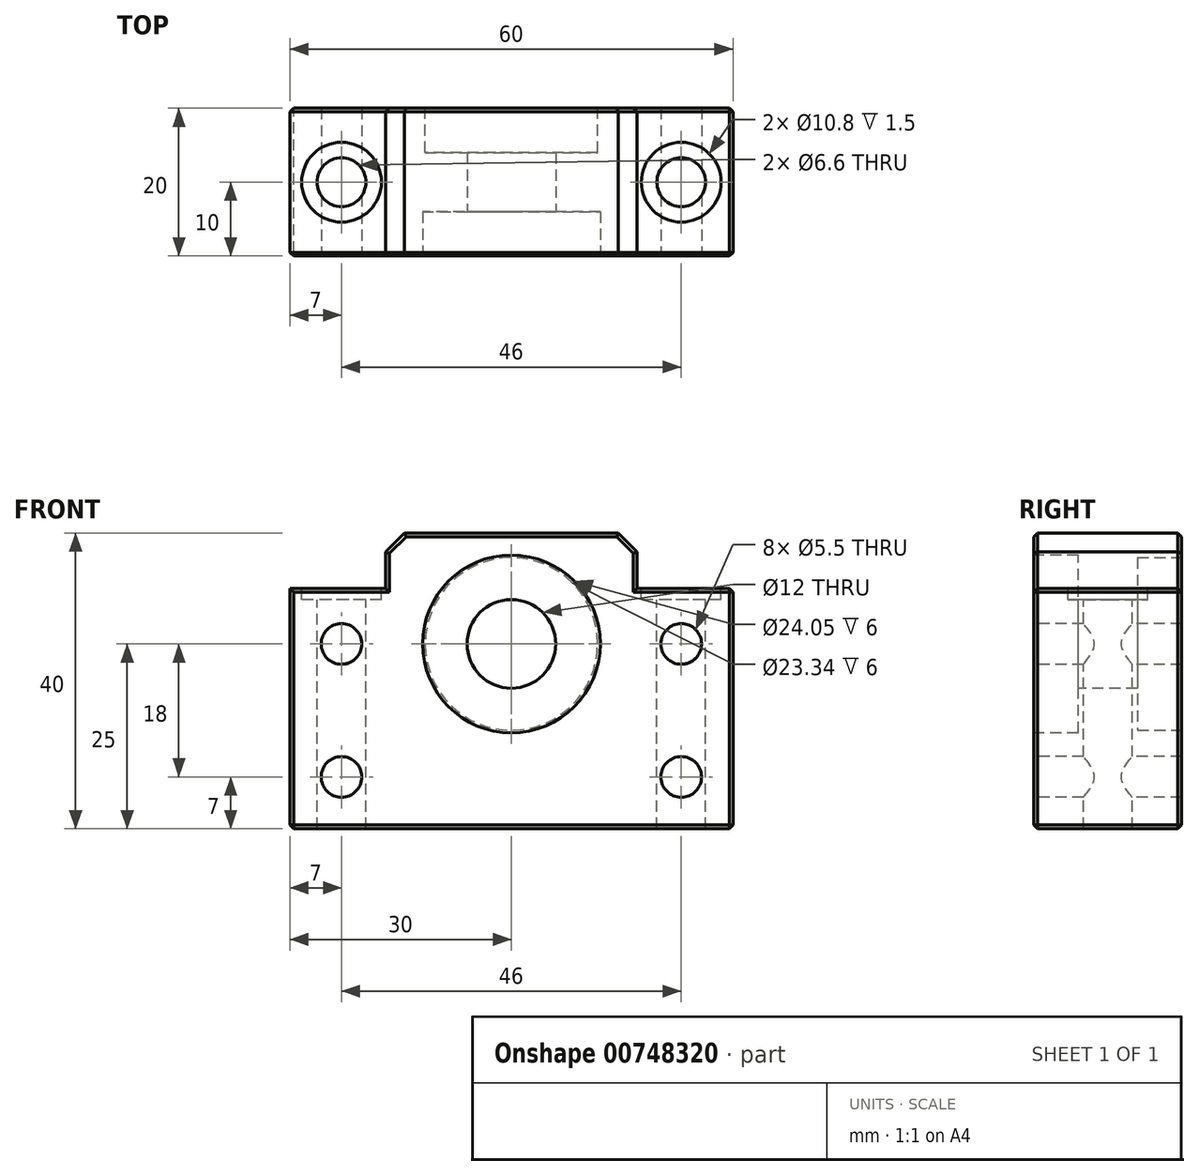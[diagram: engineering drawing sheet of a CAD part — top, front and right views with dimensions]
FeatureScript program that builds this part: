
annotation { "Feature Type Name" : "Feature", "Feature Type Description" : "" }
export const myFeature = defineFeature(function(context is Context, id is Id, definition is map)
    precondition{}
    {
        {
            var Q0;
            Q0=qCreatedBy(makeId("Front.planeOp"),FACE);
            var sketch = newSketch(context, id + "F0", { "sketchPlane" : qUnion([Q0])});
            skLineSegment(sketch, "E0.bottom", {"start": v(30, -16.25) * mm, "end": v(-30, -16.25) * mm});
            skLineSegment(sketch, "E0.top", {"start": v(30, 16.25) * mm, "end": v(17, 16.25) * mm});
            skLineSegment(sketch, "E0.left", {"start": v(30, -16.25) * mm, "end": v(30, 16.25) * mm});
            skLineSegment(sketch, "E0.right", {"start": v(-30, -16.25) * mm, "end": v(-30, 16.25) * mm});
            skPoint(sketch, "E0.middle", {"position": v(0, 0) * mm});
            skLineSegment(sketch, "E1.bottom", {"start": v(17, 23.75) * mm, "end": v(-17, 23.75) * mm});
            skLineSegment(sketch, "E1.left", {"start": v(17, 23.75) * mm, "end": v(17, 16.25) * mm});
            skLineSegment(sketch, "E1.right", {"start": v(-17, 23.75) * mm, "end": v(-17, 16.25) * mm});
            skPoint(sketch, "E1.middle", {"position": v(0, 16.25) * mm});
            skLineSegment(sketch, "E2.trimOffspring", {"start": v(-17, 16.25) * mm, "end": v(-30, 16.25) * mm});
            skSolve(sketch);
        }
        {
            var Q0;
            Q0 = qSketchRegion(id + "F0", true);
            extrude(context, id + "F1", {"entities" : qUnion([Q0]), "depth" : 20 * mm, "offsetDistance" : 25.4 * mm});
        }
        {
            var Q0;
            Q0=makeQuery(id+"F1.opExtrude","CAP_FACE",FACE,{"disambiguationData":[OSD([sQuery(id+"F0.wireOp",EDGE,"E0.bottom"),sQuery(id+"F0.wireOp",EDGE,"E0.top"),sQuery(id+"F0.wireOp",EDGE,"E0.left"),sQuery(id+"F0.wireOp",EDGE,"E0.right"),sQuery(id+"F0.wireOp",EDGE,"E1.bottom"),sQuery(id+"F0.wireOp",EDGE,"E1.left"),sQuery(id+"F0.wireOp",EDGE,"E1.right"),sQuery(id+"F0.wireOp",EDGE,"E2.trimOffspring")])],"isStart":false});
            var sketch = newSketch(context, id + "F2", { "sketchPlane" : qUnion([Q0])});
            skLineSegment(sketch, "E3", {"start": v(0, 23.75) * mm, "end": v(0, -16.25) * mm, "construction": true});
            skLineSegment(sketch, "E4.0", {"start": v(-23, 23.75) * mm, "end": v(-23, -16.25) * mm, "construction": true});
            skLineSegment(sketch, "E5.0", {"start": v(23, 23.75) * mm, "end": v(23, -16.25) * mm, "construction": true});
            skLineSegment(sketch, "E6", {"start": v(-30, 8.75) * mm, "end": v(30, 8.75) * mm, "construction": true});
            skLineSegment(sketch, "E7", {"start": v(30, -9.25) * mm, "end": v(-30, -9.25) * mm, "construction": true});
            skCircle(sketch, "E8", {"center": v(0, 8.75) * mm, "radius": 6 * mm});
            skCircle(sketch, "E9", {"center": v(-23, 8.75) * mm, "radius": 2.75 * mm});
            skCircle(sketch, "E10", {"center": v(-23, -9.25) * mm, "radius": 2.75 * mm});
            skCircle(sketch, "E11", {"center": v(23, 8.75) * mm, "radius": 2.75 * mm});
            skCircle(sketch, "E12", {"center": v(23, -9.25) * mm, "radius": 2.75 * mm});
            skSolve(sketch);
        }
        {
            var Q0;
            Q0 = qSketchRegion(id + "F2", true);
            extrude(context, id + "F3", {"entities" : qUnion([Q0]), "operationType" : NewBodyOperationType.REMOVE, "endBound" : BoundingType.THROUGH_ALL, "oppositeDirection" : true, "depth" : 25.4 * mm, "offsetDistance" : 25.4 * mm});
        }
        {
            var Q0;
            Q0=makeQuery(id+"F1.opExtrude","SWEPT_FACE",FACE,{"disambiguationData":[OSD([sQuery(id+"F0.wireOp",EDGE,"E2.trimOffspring")])]});
            var sketch = newSketch(context, id + "F4", { "sketchPlane" : qUnion([Q0])});
            skLineSegment(sketch, "E13", {"start": v(-30, -10) * mm, "end": v(29.98, -10) * mm, "construction": true});
            skLineSegment(sketch, "E14", {"start": v(0, -10) * mm, "end": v(0, 0) * mm, "construction": true});
            skLineSegment(sketch, "E15.0", {"start": v(23, -10) * mm, "end": v(23, 0) * mm, "construction": true});
            skLineSegment(sketch, "E16.0", {"start": v(-23, -10) * mm, "end": v(-23, 0) * mm, "construction": true});
            skCircle(sketch, "E17", {"center": v(-23, -10) * mm, "radius": 5.4 * mm});
            skCircle(sketch, "E18", {"center": v(23, -10) * mm, "radius": 5.4 * mm});
            skSolve(sketch);
        }
        {
            var Q0;
            Q0 = qSketchRegion(id + "F4", true);
            extrude(context, id + "F5", {"entities" : qUnion([Q0]), "operationType" : NewBodyOperationType.REMOVE, "oppositeDirection" : true, "depth" : 1.5 * mm, "offsetDistance" : 25.4 * mm});
        }
        {
            var Q0;
            Q0=makeQuery(id+"F5.boolean.opBoolean","COPY",FACE,{"derivedFrom":makeQuery(id+"F5.opExtrude","CAP_FACE",FACE,{"disambiguationData":[OSD([sQuery(id+"F4.wireOp",EDGE,"E17")])],"isStart":false})});
            var sketch = newSketch(context, id + "F6", { "sketchPlane" : qUnion([Q0])});
            skLineSegment(sketch, "E19", {"start": v(-23, -10) * mm, "end": v(29.58, -10) * mm, "construction": true});
            skLineSegment(sketch, "E20", {"start": v(-23, -10) * mm, "end": v(-23, -7.1) * mm, "construction": true});
            skLineSegment(sketch, "E21.0", {"start": v(23, -10) * mm, "end": v(23, -7.1) * mm, "construction": true});
            skCircle(sketch, "E22", {"center": v(-23, -10) * mm, "radius": 3.3 * mm});
            skCircle(sketch, "E23", {"center": v(23, -10) * mm, "radius": 3.3 * mm});
            skSolve(sketch);
        }
        {
            var Q0;
            Q0 = qSketchRegion(id + "F6", true);
            extrude(context, id + "F7", {"entities" : qUnion([Q0]), "operationType" : NewBodyOperationType.REMOVE, "endBound" : BoundingType.THROUGH_ALL, "oppositeDirection" : true, "depth" : 25.4 * mm, "offsetDistance" : 25.4 * mm});
        }
        {
            var Q0;
            Q0=makeQuery(id+"F1.opExtrude","CAP_FACE",FACE,{"disambiguationData":[OSD([sQuery(id+"F0.wireOp",EDGE,"E0.bottom"),sQuery(id+"F0.wireOp",EDGE,"E0.top"),sQuery(id+"F0.wireOp",EDGE,"E0.left"),sQuery(id+"F0.wireOp",EDGE,"E0.right"),sQuery(id+"F0.wireOp",EDGE,"E1.bottom"),sQuery(id+"F0.wireOp",EDGE,"E1.left"),sQuery(id+"F0.wireOp",EDGE,"E1.right"),sQuery(id+"F0.wireOp",EDGE,"E2.trimOffspring")])],"isStart":false});
            var sketch = newSketch(context, id + "F8", { "sketchPlane" : qUnion([Q0])});
            skCircle(sketch, "E24", {"center": v(0, 8.75) * mm, "radius": 12.03 * mm});
            skSolve(sketch);
        }
        {
            var Q0;
            Q0 = qSketchRegion(id + "F8", true);
            extrude(context, id + "F9", {"entities" : qUnion([Q0]), "operationType" : NewBodyOperationType.REMOVE, "oppositeDirection" : true, "depth" : 6 * mm, "offsetDistance" : 25.4 * mm});
        }
        {
            var Q0;
            Q0=makeQuery(id+"F1.opExtrude","CAP_FACE",FACE,{"disambiguationData":[OSD([sQuery(id+"F0.wireOp",EDGE,"E0.bottom"),sQuery(id+"F0.wireOp",EDGE,"E0.top"),sQuery(id+"F0.wireOp",EDGE,"E0.left"),sQuery(id+"F0.wireOp",EDGE,"E0.right"),sQuery(id+"F0.wireOp",EDGE,"E1.bottom"),sQuery(id+"F0.wireOp",EDGE,"E1.left"),sQuery(id+"F0.wireOp",EDGE,"E1.right"),sQuery(id+"F0.wireOp",EDGE,"E2.trimOffspring")])],"isStart":true});
            var sketch = newSketch(context, id + "F10", { "sketchPlane" : qUnion([Q0])});
            skCircle(sketch, "E25", {"center": v(0, 8.75) * mm, "radius": 11.67 * mm});
            skSolve(sketch);
        }
        {
            var Q0;
            Q0 = qSketchRegion(id + "F10", true);
            extrude(context, id + "F11", {"entities" : qUnion([Q0]), "operationType" : NewBodyOperationType.REMOVE, "oppositeDirection" : true, "depth" : 6 * mm, "offsetDistance" : 25.4 * mm});
        }
        {
            var Q0;
            Q0=makeQuery(id+"F1.opExtrude","SWEPT_EDGE",EDGE,{"disambiguationData":[OSD([sQuery(id+"F0.wireOp",EDGE,"E1.bottom"),sQuery(id+"F0.wireOp",EDGE,"E1.left")])]});
            var Q1;
            Q1=makeQuery(id+"F1.opExtrude","SWEPT_EDGE",EDGE,{"disambiguationData":[OSD([sQuery(id+"F0.wireOp",EDGE,"E1.bottom"),sQuery(id+"F0.wireOp",EDGE,"E1.right")])]});
            chamfer(context, id + "F12", {"entities" : qUnion([Q0, Q1]), "width" : 2.54 * mm, "tangentPropagation" : true});
        }
        {
            var Q0;
            Q0=makeQuery(id+"F1.opExtrude","CAP_EDGE",EDGE,{"disambiguationData":[OSD([sQuery(id+"F0.wireOp",EDGE,"E0.top")])],"isStart":true});
            var Q1;
            Q1=makeQuery(id+"F1.opExtrude","CAP_EDGE",EDGE,{"disambiguationData":[OSD([sQuery(id+"F0.wireOp",EDGE,"E1.left")])],"isStart":true});
            var Q2;
            {var subQ0=sQuery(id+"F0.wireOp",EDGE,"E1.left");var subQ1=sQuery(id+"F0.wireOp",EDGE,"E1.bottom");Q2=makeQuery(id+"F12.opChamfer","BLEND_EDGE",EDGE,{"blendedFrom":[makeQuery(id+"F1.opExtrude","SWEPT_EDGE",EDGE,{"disambiguationData":[OSD([subQ1,subQ0])]}),makeQuery(id+"F1.opExtrude","CAP_FACE",FACE,{"disambiguationData":[OSD([sQuery(id+"F0.wireOp",EDGE,"E0.bottom"),sQuery(id+"F0.wireOp",EDGE,"E0.top"),sQuery(id+"F0.wireOp",EDGE,"E0.left"),sQuery(id+"F0.wireOp",EDGE,"E0.right"),subQ1,subQ0,sQuery(id+"F0.wireOp",EDGE,"E1.right"),sQuery(id+"F0.wireOp",EDGE,"E2.trimOffspring")])],"isStart":true})],"blendedInto":[makeQuery(id+"F1.opExtrude","CAP_FACE",FACE,{"disambiguationData":[OSD([sQuery(id+"F0.wireOp",EDGE,"E0.bottom"),sQuery(id+"F0.wireOp",EDGE,"E0.top"),sQuery(id+"F0.wireOp",EDGE,"E0.left"),sQuery(id+"F0.wireOp",EDGE,"E0.right"),subQ1,subQ0,sQuery(id+"F0.wireOp",EDGE,"E1.right"),sQuery(id+"F0.wireOp",EDGE,"E2.trimOffspring")])],"isStart":true})]});}
            var Q3;
            Q3=makeQuery(id+"F1.opExtrude","CAP_EDGE",EDGE,{"disambiguationData":[OSD([sQuery(id+"F0.wireOp",EDGE,"E1.bottom")])],"isStart":true});
            var Q4;
            {var subQ0=sQuery(id+"F0.wireOp",EDGE,"E1.right");var subQ1=sQuery(id+"F0.wireOp",EDGE,"E1.bottom");Q4=makeQuery(id+"F12.opChamfer","BLEND_EDGE",EDGE,{"blendedFrom":[makeQuery(id+"F1.opExtrude","SWEPT_EDGE",EDGE,{"disambiguationData":[OSD([subQ1,subQ0])]}),makeQuery(id+"F1.opExtrude","CAP_FACE",FACE,{"disambiguationData":[OSD([sQuery(id+"F0.wireOp",EDGE,"E0.bottom"),sQuery(id+"F0.wireOp",EDGE,"E0.top"),sQuery(id+"F0.wireOp",EDGE,"E0.left"),sQuery(id+"F0.wireOp",EDGE,"E0.right"),subQ1,sQuery(id+"F0.wireOp",EDGE,"E1.left"),subQ0,sQuery(id+"F0.wireOp",EDGE,"E2.trimOffspring")])],"isStart":true})],"blendedInto":[makeQuery(id+"F1.opExtrude","CAP_FACE",FACE,{"disambiguationData":[OSD([sQuery(id+"F0.wireOp",EDGE,"E0.bottom"),sQuery(id+"F0.wireOp",EDGE,"E0.top"),sQuery(id+"F0.wireOp",EDGE,"E0.left"),sQuery(id+"F0.wireOp",EDGE,"E0.right"),subQ1,sQuery(id+"F0.wireOp",EDGE,"E1.left"),subQ0,sQuery(id+"F0.wireOp",EDGE,"E2.trimOffspring")])],"isStart":true})]});}
            var Q5;
            Q5=makeQuery(id+"F1.opExtrude","CAP_EDGE",EDGE,{"disambiguationData":[OSD([sQuery(id+"F0.wireOp",EDGE,"E1.right")])],"isStart":true});
            var Q6;
            Q6=makeQuery(id+"F1.opExtrude","CAP_EDGE",EDGE,{"disambiguationData":[OSD([sQuery(id+"F0.wireOp",EDGE,"E2.trimOffspring")])],"isStart":true});
            var Q7;
            Q7=makeQuery(id+"F1.opExtrude","CAP_EDGE",EDGE,{"disambiguationData":[OSD([sQuery(id+"F0.wireOp",EDGE,"E0.right")])],"isStart":true});
            var Q8;
            Q8=makeQuery(id+"F1.opExtrude","CAP_EDGE",EDGE,{"disambiguationData":[OSD([sQuery(id+"F0.wireOp",EDGE,"E0.bottom")])],"isStart":true});
            var Q9;
            Q9=makeQuery(id+"F1.opExtrude","CAP_EDGE",EDGE,{"disambiguationData":[OSD([sQuery(id+"F0.wireOp",EDGE,"E0.left")])],"isStart":true});
            var Q10;
            Q10=makeQuery(id+"F1.opExtrude","SWEPT_EDGE",EDGE,{"disambiguationData":[OSD([sQuery(id+"F0.wireOp",EDGE,"E0.top"),sQuery(id+"F0.wireOp",EDGE,"E0.left")])]});
            var Q11;
            Q11=makeQuery(id+"F1.opExtrude","CAP_EDGE",EDGE,{"disambiguationData":[OSD([sQuery(id+"F0.wireOp",EDGE,"E0.left")])],"isStart":false});
            var Q12;
            Q12=makeQuery(id+"F1.opExtrude","SWEPT_EDGE",EDGE,{"disambiguationData":[OSD([sQuery(id+"F0.wireOp",EDGE,"E0.bottom"),sQuery(id+"F0.wireOp",EDGE,"E0.left")])]});
            var Q13;
            Q13=makeQuery(id+"F1.opExtrude","CAP_EDGE",EDGE,{"disambiguationData":[OSD([sQuery(id+"F0.wireOp",EDGE,"E0.top")])],"isStart":false});
            var Q14;
            Q14=makeQuery(id+"F1.opExtrude","CAP_EDGE",EDGE,{"disambiguationData":[OSD([sQuery(id+"F0.wireOp",EDGE,"E1.left")])],"isStart":false});
            var Q15;
            {var subQ0=sQuery(id+"F0.wireOp",EDGE,"E1.left");var subQ1=sQuery(id+"F0.wireOp",EDGE,"E1.bottom");Q15=makeQuery(id+"F12.opChamfer","BLEND_EDGE",EDGE,{"blendedFrom":[makeQuery(id+"F1.opExtrude","SWEPT_EDGE",EDGE,{"disambiguationData":[OSD([subQ1,subQ0])]}),makeQuery(id+"F1.opExtrude","CAP_FACE",FACE,{"disambiguationData":[OSD([sQuery(id+"F0.wireOp",EDGE,"E0.bottom"),sQuery(id+"F0.wireOp",EDGE,"E0.top"),sQuery(id+"F0.wireOp",EDGE,"E0.left"),sQuery(id+"F0.wireOp",EDGE,"E0.right"),subQ1,subQ0,sQuery(id+"F0.wireOp",EDGE,"E1.right"),sQuery(id+"F0.wireOp",EDGE,"E2.trimOffspring")])],"isStart":false})],"blendedInto":[makeQuery(id+"F1.opExtrude","CAP_FACE",FACE,{"disambiguationData":[OSD([sQuery(id+"F0.wireOp",EDGE,"E0.bottom"),sQuery(id+"F0.wireOp",EDGE,"E0.top"),sQuery(id+"F0.wireOp",EDGE,"E0.left"),sQuery(id+"F0.wireOp",EDGE,"E0.right"),subQ1,subQ0,sQuery(id+"F0.wireOp",EDGE,"E1.right"),sQuery(id+"F0.wireOp",EDGE,"E2.trimOffspring")])],"isStart":false})]});}
            var Q16;
            Q16=makeQuery(id+"F1.opExtrude","CAP_EDGE",EDGE,{"disambiguationData":[OSD([sQuery(id+"F0.wireOp",EDGE,"E1.bottom")])],"isStart":false});
            var Q17;
            {var subQ0=sQuery(id+"F0.wireOp",EDGE,"E1.right");var subQ1=sQuery(id+"F0.wireOp",EDGE,"E1.bottom");Q17=makeQuery(id+"F12.opChamfer","BLEND_EDGE",EDGE,{"blendedFrom":[makeQuery(id+"F1.opExtrude","SWEPT_EDGE",EDGE,{"disambiguationData":[OSD([subQ1,subQ0])]}),makeQuery(id+"F1.opExtrude","CAP_FACE",FACE,{"disambiguationData":[OSD([sQuery(id+"F0.wireOp",EDGE,"E0.bottom"),sQuery(id+"F0.wireOp",EDGE,"E0.top"),sQuery(id+"F0.wireOp",EDGE,"E0.left"),sQuery(id+"F0.wireOp",EDGE,"E0.right"),subQ1,sQuery(id+"F0.wireOp",EDGE,"E1.left"),subQ0,sQuery(id+"F0.wireOp",EDGE,"E2.trimOffspring")])],"isStart":false})],"blendedInto":[makeQuery(id+"F1.opExtrude","CAP_FACE",FACE,{"disambiguationData":[OSD([sQuery(id+"F0.wireOp",EDGE,"E0.bottom"),sQuery(id+"F0.wireOp",EDGE,"E0.top"),sQuery(id+"F0.wireOp",EDGE,"E0.left"),sQuery(id+"F0.wireOp",EDGE,"E0.right"),subQ1,sQuery(id+"F0.wireOp",EDGE,"E1.left"),subQ0,sQuery(id+"F0.wireOp",EDGE,"E2.trimOffspring")])],"isStart":false})]});}
            var Q18;
            Q18=makeQuery(id+"F1.opExtrude","CAP_EDGE",EDGE,{"disambiguationData":[OSD([sQuery(id+"F0.wireOp",EDGE,"E1.right")])],"isStart":false});
            var Q19;
            Q19=makeQuery(id+"F1.opExtrude","CAP_EDGE",EDGE,{"disambiguationData":[OSD([sQuery(id+"F0.wireOp",EDGE,"E2.trimOffspring")])],"isStart":false});
            var Q20;
            Q20=makeQuery(id+"F1.opExtrude","CAP_EDGE",EDGE,{"disambiguationData":[OSD([sQuery(id+"F0.wireOp",EDGE,"E0.right")])],"isStart":false});
            var Q21;
            Q21=makeQuery(id+"F1.opExtrude","SWEPT_EDGE",EDGE,{"disambiguationData":[OSD([sQuery(id+"F0.wireOp",EDGE,"E0.bottom"),sQuery(id+"F0.wireOp",EDGE,"E0.right")])]});
            var Q22;
            Q22=makeQuery(id+"F1.opExtrude","CAP_EDGE",EDGE,{"disambiguationData":[OSD([sQuery(id+"F0.wireOp",EDGE,"E0.bottom")])],"isStart":false});
            chamfer(context, id + "F13", {"entities" : qUnion([Q0, Q1, Q2, Q3, Q4, Q5, Q6, Q7, Q8, Q9, Q10, Q11, Q12, Q13, Q14, Q15, Q16, Q17, Q18, Q19, Q20, Q21, Q22]), "width" : .5 * mm, "tangentPropagation" : true});
        }
    });
